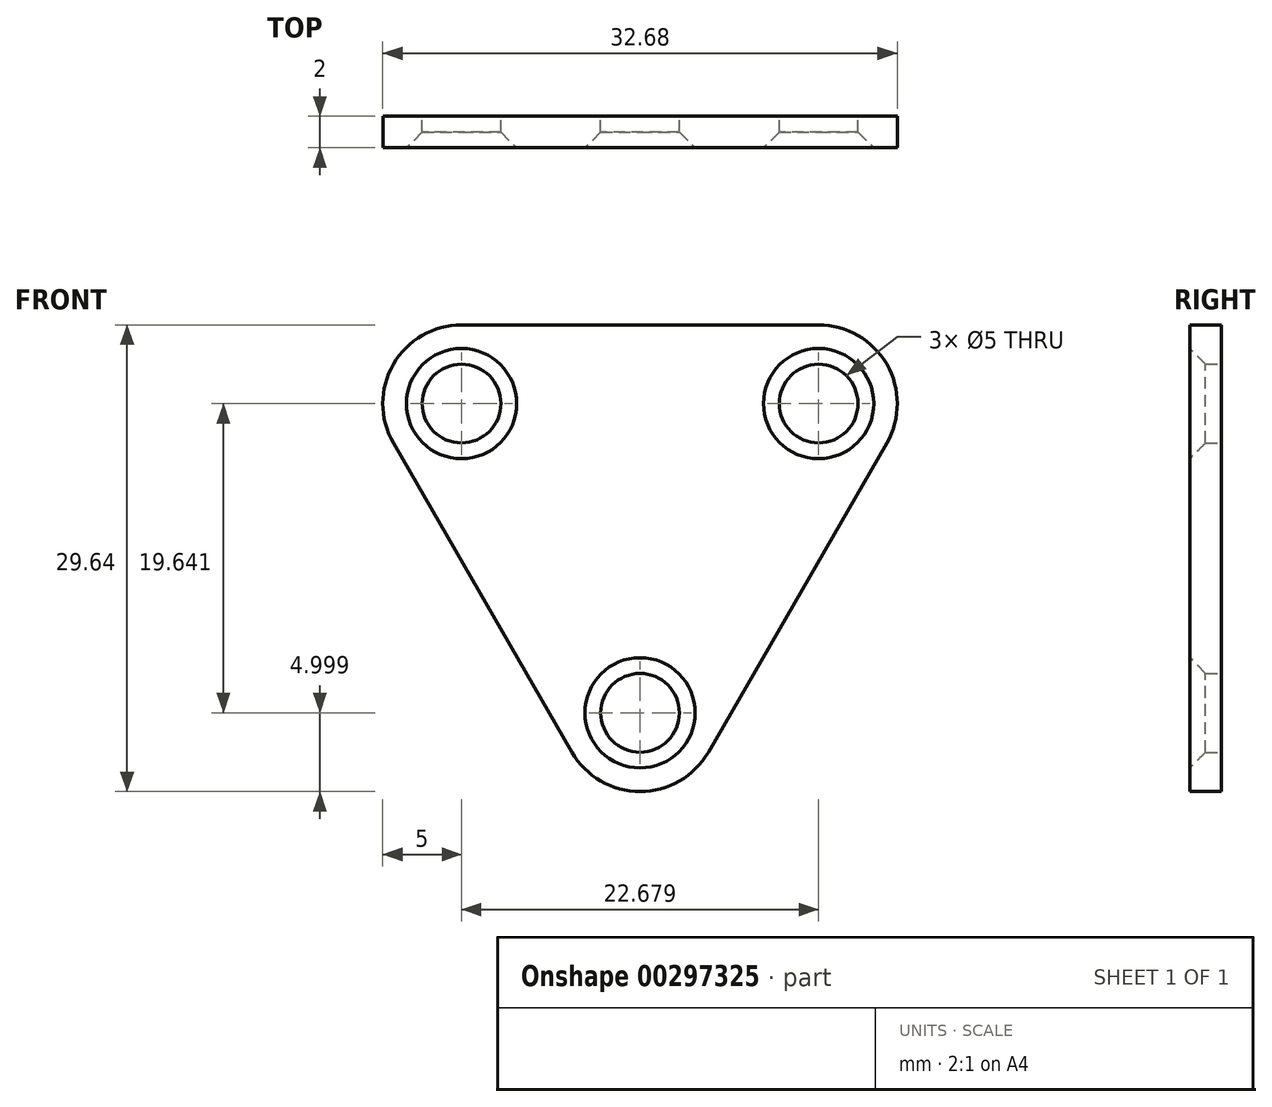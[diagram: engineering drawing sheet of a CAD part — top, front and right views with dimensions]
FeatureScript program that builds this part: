
annotation { "Feature Type Name" : "Feature", "Feature Type Description" : "" }
export const myFeature = defineFeature(function(context is Context, id is Id, definition is map)
    precondition{}
    {
        {
            var Q0;
            Q0=qCreatedBy(makeId("Front.planeOp"),FACE);
            var sketch = newSketch(context, id + "F0", { "sketchPlane" : qUnion([Q0])});
            skCircle(sketch, "E0", {"center": v(-11.34, -5) * mm, "radius": 2.5 * mm});
            skCircle(sketch, "E1", {"center": v(11.34, -5) * mm, "radius": 2.5 * mm});
            skCircle(sketch, "E2", {"center": v(0, -24.64) * mm, "radius": 2.5 * mm});
            skLineSegment(sketch, "E3.0", {"start": v(-11.34, -5) * mm, "end": v(11.34, -5) * mm, "construction": true});
            skLineSegment(sketch, "E3.1", {"start": v(0, -24.64) * mm, "end": v(-11.34, -5) * mm, "construction": true});
            skLineSegment(sketch, "E3.2", {"start": v(11.34, -5) * mm, "end": v(0, -24.64) * mm, "construction": true});
            skPoint(sketch, "E4.visualSharp", {"position": v(-22.5, 0) * mm});
            skPoint(sketch, "E5.visualSharp", {"position": v(22.5, 0) * mm});
            skLineSegment(sketch, "E6.0", {"start": v(20, 0) * mm, "end": v(0, -34.64) * mm});
            skLineSegment(sketch, "E6.1", {"start": v(-20, 0) * mm, "end": v(20, 0) * mm});
            skLineSegment(sketch, "E6.2", {"start": v(0, -34.64) * mm, "end": v(-20, 0) * mm});
            skSolve(sketch);
        }
        {
            var Q0;
            Q0 = qSketchRegion(id + "F0", true);
            extrude(context, id + "F1", {"entities" : qUnion([Q0]), "depth" : 2 * mm});
        }
        {
            var Q0;
            Q0=makeQuery(id+"F1.opExtrude","SWEPT_EDGE",EDGE,{"disambiguationData":[OSD([sQuery(id+"F0.wireOp",EDGE,"E6.1"),sQuery(id+"F0.wireOp",EDGE,"E6.2")])]});
            var Q1;
            Q1=makeQuery(id+"F1.opExtrude","SWEPT_EDGE",EDGE,{"disambiguationData":[OSD([sQuery(id+"F0.wireOp",EDGE,"E6.0"),sQuery(id+"F0.wireOp",EDGE,"E6.2")])]});
            var Q2;
            Q2=makeQuery(id+"F1.opExtrude","SWEPT_EDGE",EDGE,{"disambiguationData":[OSD([sQuery(id+"F0.wireOp",EDGE,"E6.0"),sQuery(id+"F0.wireOp",EDGE,"E6.1")])]});
            fillet(context, id + "F2", {"entities" : qUnion([Q0, Q1, Q2]), "radius" : 5 * mm, "tangentPropagation" : true, "allowEdgeOverflow" : false});
        }
        {
            var Q0;
            Q0=makeQuery(id+"F1.opExtrude","CAP_EDGE",EDGE,{"disambiguationData":[OSD([sQuery(id+"F0.wireOp",EDGE,"E0")])],"isStart":false});
            var Q1;
            Q1=makeQuery(id+"F1.opExtrude","CAP_EDGE",EDGE,{"disambiguationData":[OSD([sQuery(id+"F0.wireOp",EDGE,"E1")])],"isStart":false});
            var Q2;
            Q2=makeQuery(id+"F1.opExtrude","CAP_EDGE",EDGE,{"disambiguationData":[OSD([sQuery(id+"F0.wireOp",EDGE,"E2")])],"isStart":false});
            chamfer(context, id + "F3", {"entities" : qUnion([Q0, Q1, Q2]), "width" : 1 * mm, "tangentPropagation" : true});
        }
    });
